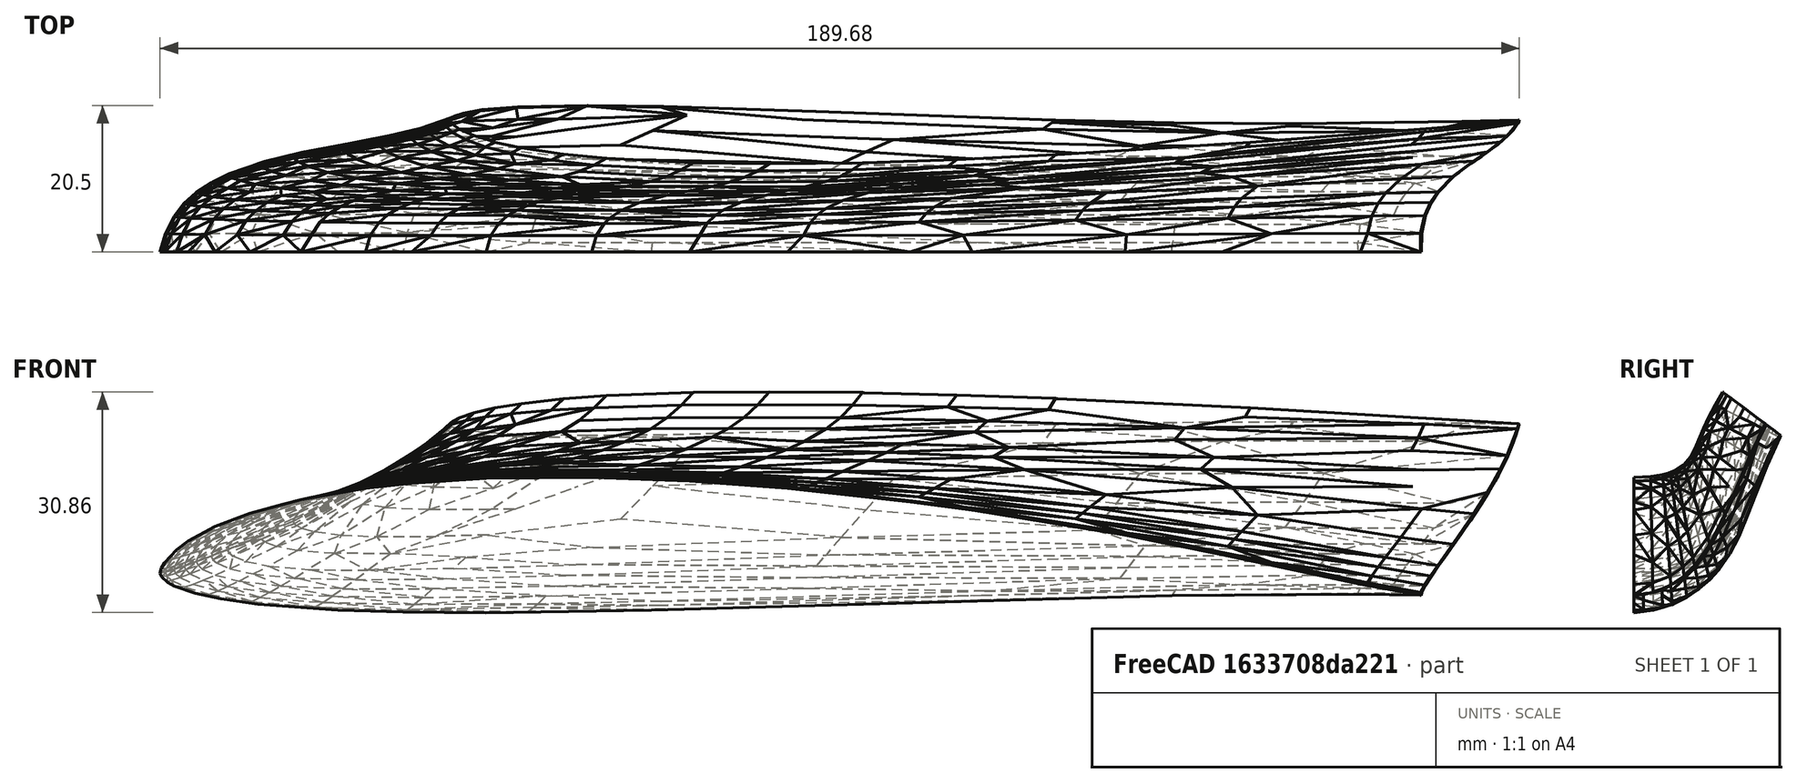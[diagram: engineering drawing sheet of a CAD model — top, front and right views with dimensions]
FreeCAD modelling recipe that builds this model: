
FCSTD DOCUMENT  (FreeCAD 0.19R24276 (Git))
Label: Con_right_winglet_alternative
License: All rights reserved
LicenseURL: http://en.wikipedia.org/wiki/All_rights_reserved
objects: Mesh::Feature×1, Part::Feature×1, Sketcher::SketchObject×1, PartDesign::Body×1, Part::Extrusion×1, Part::MultiCommon×1
note: 5 computed .brp shape members not serialized (recipe doc carries the construction recipe); baked Part::Feature solids carry a one-line shape summary decoded from their .brp

FEATURE [Mesh::Feature] Con_right_winglet_alternative
FEATURE [Part::Feature] Con_right_winglet_alternative001
  shape: bbox 222.2 x 75.89 x 139.7 mm, 1118 faces, 0 solids (baked)
FEATURE [Sketcher::SketchObject] Sketch
  FullyConstrained = true
  MapMode = 5
  Placement = pos=(0,0,0) rot=(0.57735,0.57735,0.57735;2.0944rad)
  Support = -> [YZ_Plane]
  sketch-geometry (5):
    g0: LineSegment StartX=931.97 StartY=60.04 StartZ=0 EndX=953.07 EndY=44.14 EndZ=0
    g1: LineSegment StartX=953.07 StartY=44.14 StartZ=0 EndX=953.07 EndY=15.67 EndZ=0
    g2: LineSegment StartX=953.07 StartY=15.67 StartZ=0 EndX=907.17 EndY=15.67 EndZ=0
    g3: LineSegment StartX=907.17 StartY=15.67 StartZ=0 EndX=907.17 EndY=60.04 EndZ=0
    g4: LineSegment StartX=907.17 StartY=60.04 StartZ=0 EndX=931.97 EndY=60.04 EndZ=0
  constraints (15):
    c: Coincident(g0,g1)
    c: Vertical(g1)
    c: Coincident(g1,g2)
    c: Horizontal(g2)
    c: Coincident(g2,g3)
    c: Vertical(g3)
    c: Coincident(g3,g4)
    c: Coincident(g4,g0)
    c: Horizontal(g4)
    c: Angle(g0,g-1) = 0.645772
    c: DistanceX(g-1,g2) = 907.17
    c: DistanceY(g-1,g2) = 15.67
    c: DistanceY(g3,g3) = 44.37
    c: DistanceY(g1,g1) = 28.47
    c: DistanceX(g4,g4) = 24.8
FEATURE [PartDesign::Body] Body
  Group = -> [Sketch]
  Origin = -> Origin
FEATURE [Part::Extrusion] Extrude001  label="Extrude"
  Base = -> Sketch
  Dir = (1,-1e-16,1e-16)
  DirMode = 2
  FaceMakerClass = Part::FaceMakerBullseye
  LengthFwd = 500
  LengthRev = 0
  Solid = true
  Symmetric = false
FEATURE [Part::MultiCommon] Common
  Shapes = -> [Extrude001,Con_right_winglet_alternative001]
